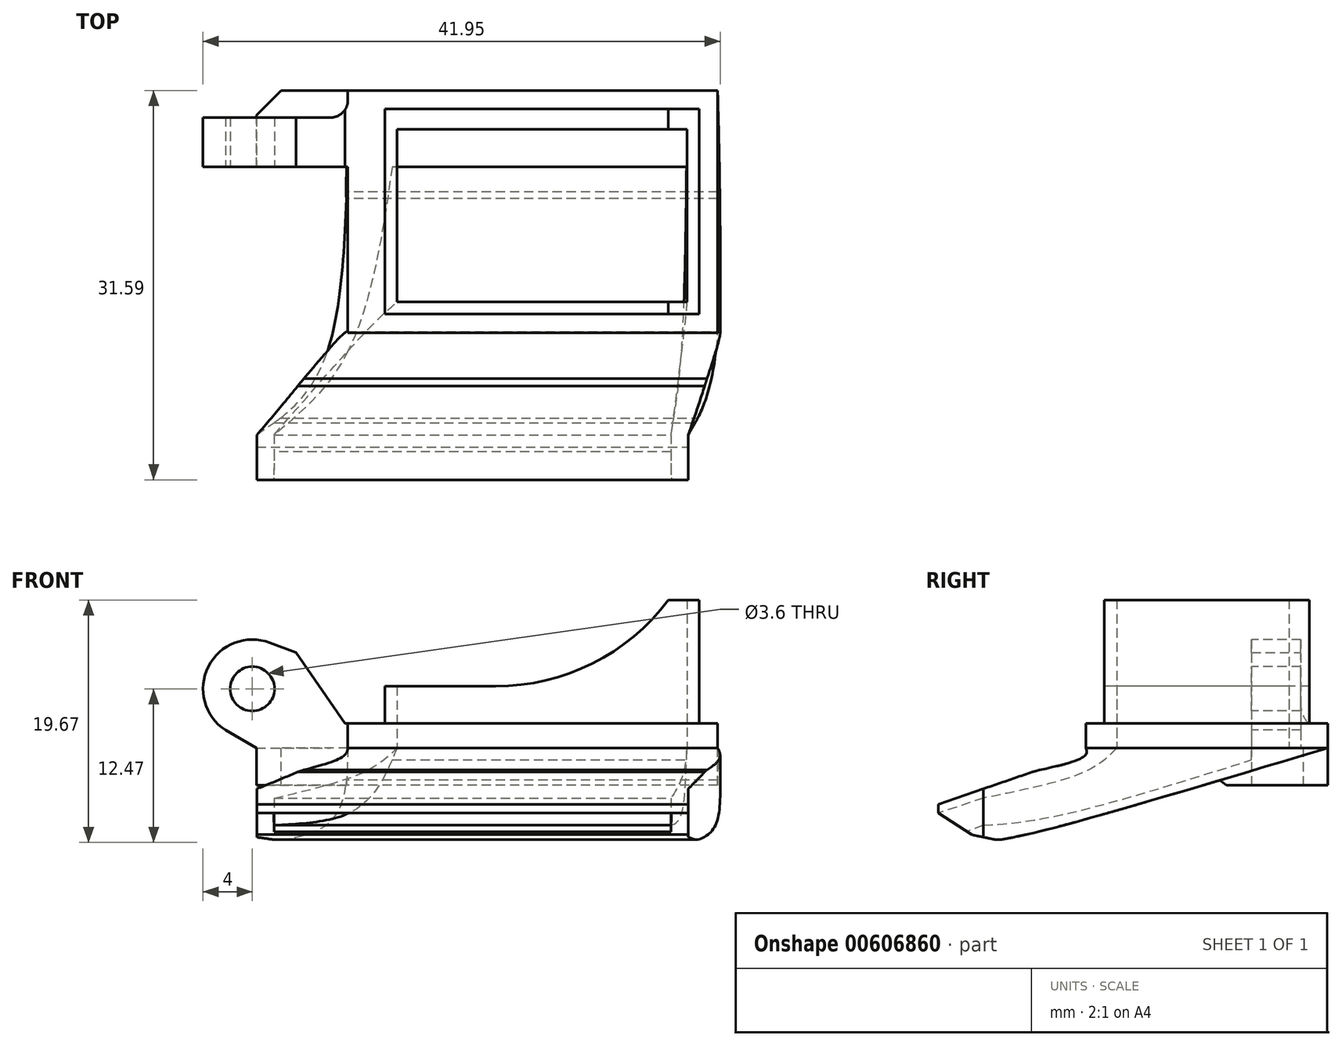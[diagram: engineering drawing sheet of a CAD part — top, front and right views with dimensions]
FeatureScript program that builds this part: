
annotation { "Feature Type Name" : "Feature", "Feature Type Description" : "" }
export const myFeature = defineFeature(function(context is Context, id is Id, definition is map)
    precondition{}
    {
        {
            var Q0;
            Q0=qCreatedBy(makeId("Top.planeOp"),FACE);
            var sketch = newSketch(context, id + "F0", { "sketchPlane" : qUnion([Q0])});
            skLineSegment(sketch, "E0.bottom", {"start": v(-12.75, 8.32) * mm, "end": v(12.75, 8.32) * mm});
            skLineSegment(sketch, "E0.top", {"start": v(-12.75, -8.32) * mm, "end": v(12.75, -8.32) * mm});
            skLineSegment(sketch, "E0.left", {"start": v(-12.75, 8.32) * mm, "end": v(-12.75, -8.32) * mm});
            skLineSegment(sketch, "E0.right", {"start": v(12.75, 8.32) * mm, "end": v(12.75, -8.32) * mm});
            skLineSegment(sketch, "E1.bottom", {"start": v(-11.75, 6.68) * mm, "end": v(11.75, 6.68) * mm});
            skLineSegment(sketch, "E1.top", {"start": v(-11.75, -7.32) * mm, "end": v(11.75, -7.32) * mm});
            skLineSegment(sketch, "E1.left", {"start": v(-11.75, 6.68) * mm, "end": v(-11.75, -7.32) * mm});
            skLineSegment(sketch, "E1.right", {"start": v(11.75, 6.68) * mm, "end": v(11.75, -7.32) * mm});
            skSolve(sketch);
        }
        {
            var Q0;
            Q0=makeQuery(id+"F0.imprint","IMPRINT",FACE,{"disambiguationData":[TD([[makeQuery(id+"F0.imprint","IMPRINT",EDGE,{"derivedFrom":sQuery(id+"F0.wireOp",EDGE,"E0.bottom")}),-1.0]])]});
            extrude(context, id + "F1", {"entities" : qUnion([Q0]), "depth" : 10 * mm, "offsetDistance" : 25 * mm});
        }
        {
            var Q0;
            Q0=makeQuery(id+"F1.opExtrude","SWEPT_FACE",FACE,{"disambiguationData":[OSD([sQuery(id+"F0.wireOp",EDGE,"E0.top")])]});
            var sketch = newSketch(context, id + "F2", { "sketchPlane" : qUnion([Q0])});
            skLineSegment(sketch, "E2", {"start": v(10.25, 10) * mm, "end": v(-3.75, 3) * mm, "construction": true});
            skLineSegment(sketch, "E3", {"start": v(-3.75, 3) * mm, "end": v(-12.75, 3) * mm});
            skArc(sketch, "E4", {"start": v(-3.75, 3) * mm, "mid": v(4.08, 4.85) * mm, "end": v(10.25, 10) * mm});
            skLineSegment(sketch, "E5", {"start": v(-12.75, 3) * mm, "end": v(-12.75, 10) * mm});
            skLineSegment(sketch, "E6", {"start": v(-12.75, 10) * mm, "end": v(10.25, 10) * mm});
            skSolve(sketch);
        }
        {
            var Q0;
            Q0=qSketchRegion(id+"F2",true);
            extrude(context, id + "F3", {"entities" : qUnion([Q0]), "operationType" : NewBodyOperationType.REMOVE, "oppositeDirection" : true, "depth" : 25 * mm, "offsetDistance" : 25 * mm});
        }
        {
            var Q0;
            Q0=makeQuery(id+"F1.opExtrude","CAP_FACE",FACE,{"disambiguationData":[OSD([sQuery(id+"F0.wireOp",EDGE,"E0.bottom"),sQuery(id+"F0.wireOp",EDGE,"E0.top"),sQuery(id+"F0.wireOp",EDGE,"E0.left"),sQuery(id+"F0.wireOp",EDGE,"E0.right"),sQuery(id+"F0.wireOp",EDGE,"E1.bottom"),sQuery(id+"F0.wireOp",EDGE,"E1.top"),sQuery(id+"F0.wireOp",EDGE,"E1.left"),sQuery(id+"F0.wireOp",EDGE,"E1.right")])],"isStart":true});
            var sketch = newSketch(context, id + "F4", { "sketchPlane" : qUnion([Q0])});
            skLineSegment(sketch, "E7.0", {"start": v(-15.75, 9.82) * mm, "end": v(14.25, 9.82) * mm});
            skLineSegment(sketch, "E7.1", {"start": v(-15.75, 9.82) * mm, "end": v(-15.75, -9.82) * mm});
            skLineSegment(sketch, "E7.2", {"start": v(-15.75, -9.82) * mm, "end": v(14.25, -9.82) * mm});
            skLineSegment(sketch, "E7.3", {"start": v(14.25, 9.82) * mm, "end": v(14.25, -9.82) * mm});
            skLineSegment(sketch, "E8.bottom", {"start": v(-11.75, -6.68) * mm, "end": v(11.75, -6.68) * mm});
            skLineSegment(sketch, "E8.top", {"start": v(-11.75, 7.32) * mm, "end": v(11.75, 7.32) * mm});
            skLineSegment(sketch, "E8.left", {"start": v(-11.75, -6.68) * mm, "end": v(-11.75, 7.32) * mm});
            skLineSegment(sketch, "E8.right", {"start": v(11.75, -6.68) * mm, "end": v(11.75, 7.32) * mm});
            skSolve(sketch);
        }
        {
            var Q0;
            Q0=qSketchRegion(id+"F4",true);
            extrude(context, id + "F5", {"entities" : qUnion([Q0]), "operationType" : NewBodyOperationType.ADD, "depth" : 2 * mm, "offsetDistance" : 25 * mm});
        }
        {
            var Q0;
            Q0=makeQuery(id+"F1.opExtrude","SWEPT_FACE",FACE,{"disambiguationData":[OSD([sQuery(id+"F0.wireOp",EDGE,"E0.top")])]});
            cPlane(context, id + "F6", {"entities" : qUnion([Q0]), "cplaneType" : CPlaneType.OFFSET, "offset" : 11.95 * mm, "oppositeDirection" : true, "width" : 150 * mm, "height" : 150 * mm});
        }
        {
            var Q0;
            Q0=qCreatedBy(id+"F6.planeOp",FACE);
            var sketch = newSketch(context, id + "F7", { "sketchPlane" : qUnion([Q0])});
            skCircle(sketch, "E9", {"center": v(-23.5, 2.8) * mm, "radius": 1.8 * mm});
            skArc(sketch, "E10", {"start": v(-22.08, 6.54) * mm, "mid": v(-27.07, 4.6) * mm, "end": v(-25.68, -0.56) * mm});
            skLineSegment(sketch, "E11", {"start": v(-12.75, 3) * mm, "end": v(-22.08, 6.54) * mm});
            skLineSegment(sketch, "E12", {"start": v(-12.75, 3) * mm, "end": v(-12.75, 0) * mm});
            skLineSegment(sketch, "E13", {"start": v(-25.68, -0.56) * mm, "end": v(-23.17, -2) * mm});
            skLineSegment(sketch, "E14", {"start": v(-23.17, -2) * mm, "end": v(-15.75, -2) * mm});
            skLineSegment(sketch, "E15", {"start": v(-12.75, 0) * mm, "end": v(-15.75, 0) * mm});
            skLineSegment(sketch, "E16", {"start": v(-15.75, 0) * mm, "end": v(-15.75, -2) * mm});
            skSolve(sketch);
        }
        {
            var Q0;
            Q0=qSketchRegion(id+"F7",true);
            extrude(context, id + "F8", {"entities" : qUnion([Q0]), "oppositeDirection" : true, "depth" : 4 * mm, "offsetDistance" : 25 * mm});
        }
        {
            var Q0;
            Q0=makeQuery(id+"F1.opExtrude","SWEPT_FACE",FACE,{"disambiguationData":[OSD([sQuery(id+"F0.wireOp",EDGE,"E0.top")])]});
            cPlane(context, id + "F9", {"entities" : qUnion([Q0]), "cplaneType" : CPlaneType.OFFSET, "offset" : 9.8 * mm, "width" : 150 * mm, "height" : 150 * mm});
        }
        {
            var Q0;
            Q0=makeQuery(id+"F21.boolean.opBoolean","MERGE",FACE,{"derivedFrom":[makeQuery(id+"F5.opExtrude","CAP_FACE",FACE,{"disambiguationData":[OSD([sQuery(id+"F4.wireOp",EDGE,"E7.0"),sQuery(id+"F4.wireOp",EDGE,"E7.1"),sQuery(id+"F4.wireOp",EDGE,"E7.2"),sQuery(id+"F4.wireOp",EDGE,"E7.3"),sQuery(id+"F4.wireOp",EDGE,"E8.bottom"),sQuery(id+"F4.wireOp",EDGE,"E8.top"),sQuery(id+"F4.wireOp",EDGE,"E8.left"),sQuery(id+"F4.wireOp",EDGE,"E8.right")])],"isStart":true})],"fromTools":[makeQuery(id+"F21.opExtrude","SWEPT_FACE",FACE,{"disambiguationData":[OSD([sQuery(id+"F20.wireOp",EDGE,"E25.bottom")])]})]});
            cPlane(context, id + "F10", {"entities" : qUnion([Q0]), "cplaneType" : CPlaneType.OFFSET, "offset" : 5 * mm, "oppositeDirection" : true, "width" : 150 * mm, "height" : 150 * mm});
        }
        {
            var Q0;
            Q0=qCreatedBy(id+"F9.planeOp",FACE);
            var sketch = newSketch(context, id + "F11", { "sketchPlane" : qUnion([Q0])});
            skLineSegment(sketch, "E17.bottom", {"start": v(-6.25, -8.67) * mm, "end": v(-21.25, -8.67) * mm});
            skLineSegment(sketch, "E17.top", {"start": v(-6.25, -3.67) * mm, "end": v(-21.25, -3.67) * mm});
            skLineSegment(sketch, "E17.left", {"start": v(-6.25, -8.67) * mm, "end": v(-6.25, -3.67) * mm});
            skLineSegment(sketch, "E17.right", {"start": v(-21.25, -8.67) * mm, "end": v(-21.25, -3.67) * mm});
            skPoint(sketch, "E17.middle", {"position": v(-13.75, -6.17) * mm});
            skLineSegment(sketch, "E18.0", {"start": v(-20.65, -8.07) * mm, "end": v(-20.65, -4.27) * mm});
            skLineSegment(sketch, "E18.1", {"start": v(-6.85, -8.07) * mm, "end": v(-20.65, -8.07) * mm});
            skLineSegment(sketch, "E18.2", {"start": v(-6.85, -8.07) * mm, "end": v(-6.85, -4.27) * mm});
            skLineSegment(sketch, "E18.3", {"start": v(-6.85, -4.27) * mm, "end": v(-20.65, -4.27) * mm});
            skSolve(sketch);
        }
        {
            var Q0;
            Q0=makeQuery(id+"F5.opExtrude","CAP_FACE",FACE,{"disambiguationData":[OSD([sQuery(id+"F4.wireOp",EDGE,"E7.0"),sQuery(id+"F4.wireOp",EDGE,"E7.1"),sQuery(id+"F4.wireOp",EDGE,"E7.2"),sQuery(id+"F4.wireOp",EDGE,"E7.3"),sQuery(id+"F4.wireOp",EDGE,"E8.bottom"),sQuery(id+"F4.wireOp",EDGE,"E8.top"),sQuery(id+"F4.wireOp",EDGE,"E8.left"),sQuery(id+"F4.wireOp",EDGE,"E8.right")])],"isStart":false});
            var sketch = newSketch(context, id + "F12", { "sketchPlane" : qUnion([Q0])});
            skLineSegment(sketch, "E19.0", {"start": v(-15.75, 9.82) * mm, "end": v(-15.75, -9.82) * mm});
            skLineSegment(sketch, "E19.3", {"start": v(-15.75, 9.82) * mm, "end": v(14.25, 9.82) * mm});
            skLineSegment(sketch, "E19.4", {"start": v(-15.75, -9.82) * mm, "end": v(14.25, -9.82) * mm});
            skLineSegment(sketch, "E19.7", {"start": v(14.25, 9.82) * mm, "end": v(14.25, -9.82) * mm});
            skSolve(sketch);
        }
        {
            var Q0;
            Q0=qCreatedBy(makeId("Front.planeOp"),FACE);
            cPlane(context, id + "F13", {"entities" : qUnion([Q0]), "cplaneType" : CPlaneType.OFFSET, "offset" : 11.3 * mm, "width" : 150 * mm, "height" : 150 * mm});
        }
        {
            var Q0;
            Q0=qCreatedBy(id+"F13.planeOp",FACE);
            var sketch = newSketch(context, id + "F14", { "sketchPlane" : qUnion([Q0])});
            skLineSegment(sketch, "E20.bottom", {"start": v(14.1, -3.25) * mm, "end": v(-17.4, -3.25) * mm});
            skLineSegment(sketch, "E20.top", {"start": v(14.1, -8.18) * mm, "end": v(-17.4, -8.18) * mm});
            skLineSegment(sketch, "E20.left", {"start": v(14.1, -3.25) * mm, "end": v(14.1, -8.18) * mm});
            skLineSegment(sketch, "E20.right", {"start": v(-17.4, -3.25) * mm, "end": v(-17.4, -8.18) * mm});
            skSolve(sketch);
        }
        {
            var Q0;
            Q0=qCreatedBy(id+"F9.planeOp",FACE);
            var sketch = newSketch(context, id + "F15", { "sketchPlane" : qUnion([Q0])});
            skLineSegment(sketch, "E21.bottom", {"start": v(-23.14, -4.67) * mm, "end": v(11.86, -4.67) * mm});
            skLineSegment(sketch, "E21.top", {"start": v(-23.14, -9.67) * mm, "end": v(11.86, -9.67) * mm});
            skLineSegment(sketch, "E21.left", {"start": v(-23.14, -4.67) * mm, "end": v(-23.14, -9.67) * mm});
            skLineSegment(sketch, "E21.right", {"start": v(11.86, -4.67) * mm, "end": v(11.86, -9.67) * mm});
            skLineSegment(sketch, "E22.0", {"start": v(-21.74, -6.07) * mm, "end": v(-21.74, -8.27) * mm, "construction": true});
            skLineSegment(sketch, "E22.1", {"start": v(-21.74, -6.07) * mm, "end": v(10.46, -6.07) * mm, "construction": true});
            skLineSegment(sketch, "E22.2", {"start": v(10.46, -6.07) * mm, "end": v(10.46, -8.27) * mm, "construction": true});
            skLineSegment(sketch, "E22.3", {"start": v(-21.74, -8.27) * mm, "end": v(10.46, -8.27) * mm, "construction": true});
            skSolve(sketch);
        }
        {
            var Q1;
            Q1=qSketchRegion(id+"F15",true);
            var Q2;
            Q2=qSketchRegion(id+"F14",true);
            var Q3;
            Q3=qSketchRegion(id+"F12",true);
            var Q4;
            Q4=sQuery(id+"F15.wireOp",VERTEX,"E21.right.start");
            var Q5;
            Q5=sQuery(id+"F14.wireOp",VERTEX,"E20.left.start");
            var Q6;
            Q6=sQuery(id+"F12.wireOp",VERTEX,"E19.7.start");
            loft(context, id + "F16", {"operationType" : NewBodyOperationType.ADD, "sheetProfilesArray" : [{ "sheetProfileEntities" : qUnion([Q1]) }, { "sheetProfileEntities" : qUnion([Q2]) }, { "sheetProfileEntities" : qUnion([Q3]) }], "matchConnections" : true, "connections" : [{ "connectionEntities" : qUnion([Q4, Q5, Q6]), "connectionEdgeQueries" : qUnion([]), "connectionEdgeParameters" : [] }]});
        }
        {
            var Q0;
            Q0=qCreatedBy(id+"F13.planeOp",FACE);
            var sketch = newSketch(context, id + "F17", { "sketchPlane" : qUnion([Q0])});
            skLineSegment(sketch, "E23.bottom", {"start": v(-15.73, -4.47) * mm, "end": v(11.32, -4.47) * mm});
            skLineSegment(sketch, "E23.top", {"start": v(-15.73, -7.32) * mm, "end": v(11.32, -7.32) * mm});
            skLineSegment(sketch, "E23.left", {"start": v(-15.73, -4.47) * mm, "end": v(-15.73, -7.32) * mm});
            skLineSegment(sketch, "E23.right", {"start": v(11.32, -4.47) * mm, "end": v(11.32, -7.32) * mm});
            skSolve(sketch);
        }
        {
            var Q0;
            Q0=makeQuery(id+"F16.opLoft","CAP_FACE",FACE,{"disambiguationData":[OSD([makeQuery(id+"F12.imprint","IMPRINT",FACE,{"disambiguationData":[TD([[makeQuery(id+"F12.imprint","IMPRINT",EDGE,{"derivedFrom":makeQuery(id+"F5.opExtrude","CAP_EDGE",EDGE,{"disambiguationData":[OSD([sQuery(id+"F4.wireOp",EDGE,"E8.bottom")])],"isStart":false})}),1.0]])]})])],"isStart":true});
            var sketch = newSketch(context, id + "F18", { "sketchPlane" : qUnion([Q0])});
            skLineSegment(sketch, "E24.bottom", {"start": v(-11.75, 6.68) * mm, "end": v(11.75, 6.68) * mm});
            skLineSegment(sketch, "E24.top", {"start": v(-11.75, -7.32) * mm, "end": v(11.75, -7.32) * mm});
            skLineSegment(sketch, "E24.left", {"start": v(-11.75, 6.68) * mm, "end": v(-11.75, -7.32) * mm});
            skLineSegment(sketch, "E24.right", {"start": v(11.75, 6.68) * mm, "end": v(11.75, -7.32) * mm});
            skSolve(sketch);
        }
        {
            var Q0;
            Q0=makeQuery(id+"F11.imprint","IMPRINT",FACE,{"disambiguationData":[TD([[makeQuery(id+"F11.imprint","IMPRINT",EDGE,{"derivedFrom":sQuery(id+"F11.wireOp",EDGE,"E17.bottom")}),-1.0]])]});
            cPlane(context, id + "F19", {"entities" : qUnion([Q0]), "cplaneType" : CPlaneType.OFFSET, "offset" : 3.65 * mm, "width" : 150 * mm, "height" : 150 * mm});
        }
        {
            var Q0;
            Q0=makeQuery(id+"F8.opExtrude","CAP_FACE",FACE,{"disambiguationData":[OSD([sQuery(id+"F7.wireOp",EDGE,"E9"),sQuery(id+"F7.wireOp",EDGE,"E10"),sQuery(id+"F7.wireOp",EDGE,"E11"),sQuery(id+"F7.wireOp",EDGE,"E12"),sQuery(id+"F7.wireOp",EDGE,"E13"),sQuery(id+"F7.wireOp",EDGE,"E14"),sQuery(id+"F7.wireOp",EDGE,"E15"),sQuery(id+"F7.wireOp",EDGE,"E16")])],"isStart":true});
            var sketch = newSketch(context, id + "F20", { "sketchPlane" : qUnion([Q0])});
            skLineSegment(sketch, "E25.bottom", {"start": v(-15.75, 0) * mm, "end": v(-12.75, 0) * mm});
            skLineSegment(sketch, "E25.top", {"start": v(-15.75, 4.97) * mm, "end": v(-12.75, 4.97) * mm});
            skLineSegment(sketch, "E25.left", {"start": v(-15.75, 0) * mm, "end": v(-15.75, 4.97) * mm});
            skLineSegment(sketch, "E25.right", {"start": v(-12.75, 0) * mm, "end": v(-12.75, 4.97) * mm});
            skSolve(sketch);
        }
        {
            var Q0;
            Q0 = qSketchRegion(id + "F20", true);
            extrude(context, id + "F21", {"entities" : qUnion([Q0]), "operationType" : NewBodyOperationType.REMOVE, "oppositeDirection" : true, "depth" : 25 * mm, "offsetDistance" : 25 * mm});
        }
        {
            var Q0;
            Q0=makeQuery(id+"F21.boolean.opBoolean","INTERSECT",EDGE,{"derivedFrom":[makeQuery(id+"F8.opExtrude","SWEPT_FACE",FACE,{"disambiguationData":[OSD([sQuery(id+"F7.wireOp",EDGE,"E11")])]}),makeQuery(id+"F21.opExtrude","SWEPT_FACE",FACE,{"disambiguationData":[OSD([sQuery(id+"F20.wireOp",EDGE,"E25.left")])]})]});
            chamfer(context, id + "F22", {"entities" : qUnion([Q0]), "width" : 6.5 * mm, "tangentPropagation" : true});
        }
        {
            var Q0;
            Q0=makeQuery(id+"F8.opExtrude","CAP_EDGE",EDGE,{"disambiguationData":[OSD([sQuery(id+"F7.wireOp",EDGE,"E16")])],"isStart":false});
            fillet(context, id + "F23", {"entities" : qUnion([Q0]), "radius" : 1.4 * mm, "tangentPropagation" : true, "allowEdgeOverflow" : false});
        }
        {
            var Q0;
            Q0=makeQuery(id+"F8.opExtrude","CAP_FACE",FACE,{"disambiguationData":[OSD([sQuery(id+"F7.wireOp",EDGE,"E9"),sQuery(id+"F7.wireOp",EDGE,"E10"),sQuery(id+"F7.wireOp",EDGE,"E11"),sQuery(id+"F7.wireOp",EDGE,"E12"),sQuery(id+"F7.wireOp",EDGE,"E13"),sQuery(id+"F7.wireOp",EDGE,"E14"),sQuery(id+"F7.wireOp",EDGE,"E15"),sQuery(id+"F7.wireOp",EDGE,"E16")])],"isStart":false});
            var sketch = newSketch(context, id + "F24", { "sketchPlane" : qUnion([Q0])});
            skLineSegment(sketch, "E26.0", {"start": v(15.75, -2) * mm, "end": v(15.75, 0) * mm, "construction": true});
            skLineSegment(sketch, "E27.0", {"start": v(23.17, -2) * mm, "end": v(19.3, -2) * mm, "construction": true});
            skLineSegment(sketch, "E28", {"start": v(15.75, -2) * mm, "end": v(23.17, -2) * mm});
            skLineSegment(sketch, "E29", {"start": v(23.17, -5.03) * mm, "end": v(15.75, -5.03) * mm});
            skLineSegment(sketch, "E30", {"start": v(15.75, -5.03) * mm, "end": v(15.75, -2) * mm});
            skLineSegment(sketch, "E31", {"start": v(23.17, -2) * mm, "end": v(23.17, -5.03) * mm});
            skSolve(sketch);
        }
        {
            var Q0;
            Q0 = qSketchRegion(id + "F24", true);
            extrude(context, id + "F25", {"entities" : qUnion([Q0]), "operationType" : NewBodyOperationType.ADD, "oppositeDirection" : true, "depth" : 4 * mm, "offsetDistance" : 25 * mm});
        }
        {
            var Q0;
            Q0=makeQuery(id+"F15.imprint","IMPRINT",FACE,{"disambiguationData":[TD([[makeQuery(id+"F15.imprint","IMPRINT",EDGE,{"derivedFrom":sQuery(id+"F15.wireOp",EDGE,"E21.bottom")}),-1.0]])]});
            var sketch = newSketch(context, id + "F26", { "sketchPlane" : qUnion([Q0])});
            skLineSegment(sketch, "E32.0", {"start": v(-21.74, -6.07) * mm, "end": v(10.46, -6.07) * mm});
            skLineSegment(sketch, "E33.0", {"start": v(-21.74, -6.07) * mm, "end": v(-21.74, -8.27) * mm});
            skLineSegment(sketch, "E34.0", {"start": v(-21.74, -8.27) * mm, "end": v(10.46, -8.27) * mm});
            skLineSegment(sketch, "E35.0", {"start": v(10.46, -6.07) * mm, "end": v(10.46, -8.27) * mm});
            skSolve(sketch);
        }
        {
            var Q1;
            Q1=makeQuery(id+"F18.imprint","IMPRINT",FACE,{"disambiguationData":[TD([[makeQuery(id+"F18.imprint","IMPRINT",EDGE,{"derivedFrom":sQuery(id+"F18.wireOp",EDGE,"E24.bottom")}),-1.0]])]});
            var Q2;
            Q2 = qSketchRegion(id + "F17", true);
            var Q3;
            Q3 = qSketchRegion(id + "F26", true);
            loft(context, id + "F27", {"operationType" : NewBodyOperationType.REMOVE, "sheetProfilesArray" : [{ "sheetProfileEntities" : qUnion([Q1]) }, { "sheetProfileEntities" : qUnion([Q2]) }, { "sheetProfileEntities" : qUnion([Q3]) }]});
        }
        {
            var Q0;
            Q0=qCreatedBy(id+"F19.planeOp",FACE);
            var sketch = newSketch(context, id + "F28", { "sketchPlane" : qUnion([Q0])});
            skLineSegment(sketch, "E36.0.0", {"start": v(-23.14, -4.67) * mm, "end": v(-23.14, -9.67) * mm});
            skLineSegment(sketch, "E36.0.1", {"start": v(-23.14, -9.67) * mm, "end": v(11.86, -9.67) * mm});
            skLineSegment(sketch, "E36.0.2", {"start": v(11.86, -9.67) * mm, "end": v(11.86, -4.67) * mm});
            skLineSegment(sketch, "E36.0.3", {"start": v(11.86, -4.67) * mm, "end": v(-23.14, -4.67) * mm});
            skSolve(sketch);
        }
        {
            var Q1;
            Q1=makeQuery(id+"F15.imprint","IMPRINT",FACE,{"disambiguationData":[TD([[makeQuery(id+"F15.imprint","IMPRINT",EDGE,{"derivedFrom":sQuery(id+"F15.wireOp",EDGE,"E21.bottom")}),-1.0]])]});
            var Q2;
            Q2=makeQuery(id+"F28.imprint","IMPRINT",FACE,{"disambiguationData":[TD([[makeQuery(id+"F28.imprint","IMPRINT",EDGE,{"derivedFrom":sQuery(id+"F28.wireOp",EDGE,"E36.0.0")}),1.0]])]});
            loft(context, id + "F29", {"operationType" : NewBodyOperationType.ADD, "sheetProfilesArray" : [{ "sheetProfileEntities" : qUnion([Q1]) }, { "sheetProfileEntities" : qUnion([Q2]) }]});
        }
        {
            var Q0;
            Q0=makeQuery(id+"F28.imprint","IMPRINT",FACE,{"disambiguationData":[TD([[makeQuery(id+"F28.imprint","IMPRINT",EDGE,{"derivedFrom":sQuery(id+"F28.wireOp",EDGE,"E36.0.0")}),1.0]])]});
            var sketch = newSketch(context, id + "F30", { "sketchPlane" : qUnion([Q0])});
            skLineSegment(sketch, "E37.bottom", {"start": v(-21.75, -7.3) * mm, "end": v(10.48, -7.3) * mm});
            skLineSegment(sketch, "E37.top", {"start": v(-21.75, -9.67) * mm, "end": v(10.48, -9.67) * mm});
            skLineSegment(sketch, "E37.left", {"start": v(-21.75, -7.3) * mm, "end": v(-21.75, -9.67) * mm});
            skLineSegment(sketch, "E37.right", {"start": v(10.48, -7.3) * mm, "end": v(10.48, -9.67) * mm});
            skSolve(sketch);
        }
        {
            var Q0;
            Q0=qCreatedBy(id+"F9.planeOp",FACE);
            var sketch = newSketch(context, id + "F31", { "sketchPlane" : qUnion([Q0])});
            skLineSegment(sketch, "E38.0", {"start": v(-21.74, -6.07) * mm, "end": v(-21.74, -8.27) * mm});
            skLineSegment(sketch, "E39.0", {"start": v(-21.74, -6.07) * mm, "end": v(10.46, -6.07) * mm});
            skLineSegment(sketch, "E40.0", {"start": v(-21.74, -8.27) * mm, "end": v(10.46, -8.27) * mm});
            skLineSegment(sketch, "E41.0", {"start": v(10.46, -6.07) * mm, "end": v(10.46, -8.27) * mm});
            skSolve(sketch);
        }
        {
            var Q1;
            Q1 = qSketchRegion(id + "F31", true);
            var Q2;
            Q2 = qSketchRegion(id + "F30", true);
            loft(context, id + "F32", {"operationType" : NewBodyOperationType.REMOVE, "sheetProfilesArray" : [{ "sheetProfileEntities" : qUnion([Q1]) }, { "sheetProfileEntities" : qUnion([Q2]) }]});
        }
        {
            var Q0;
            Q0=makeQuery(id+"F29.opLoft","SWEPT_FACE",FACE,{"disambiguationData":[OSD([sQuery(id+"F15.wireOp",EDGE,"E21.bottom"),sQuery(id+"F15.wireOp",EDGE,"E21.top"),sQuery(id+"F15.wireOp",EDGE,"E21.right"),sQuery(id+"F28.wireOp",EDGE,"E36.0.1"),sQuery(id+"F28.wireOp",EDGE,"E36.0.2"),sQuery(id+"F28.wireOp",EDGE,"E36.0.3")])]});
            var sketch = newSketch(context, id + "F33", { "sketchPlane" : qUnion([Q0])});
            skLineSegment(sketch, "E42.0", {"start": v(-21.77, -9.67) * mm, "end": v(-21.77, -7.3) * mm});
            skLineSegment(sketch, "E43.0", {"start": v(-18.12, -9.67) * mm, "end": v(-21.77, -9.67) * mm});
            skLineSegment(sketch, "E44", {"start": v(-21.77, -7.3) * mm, "end": v(-18.12, -9.67) * mm});
            skSolve(sketch);
        }
        {
            var Q0;
            Q0 = qSketchRegion(id + "F33", true);
            extrude(context, id + "F34", {"entities" : qUnion([Q0]), "operationType" : NewBodyOperationType.REMOVE, "endBound" : BoundingType.UP_TO_NEXT, "oppositeDirection" : true, "depth" : 25 * mm, "offsetDistance" : 25 * mm});
        }
        {
            var Q0;
            {var subQ0=sQuery(id+"F15.wireOp",EDGE,"E21.right");var subQ1=sQuery(id+"F15.wireOp",EDGE,"E21.top");var subQ2=sQuery(id+"F15.wireOp",EDGE,"E21.left");Q0=makeQuery(id+"F34.boolean.opBoolean","MERGE",EDGE,{"derivedFrom":[makeQuery(id+"F29.boolean.opBoolean","MERGE",EDGE,{"derivedFrom":[makeQuery(id+"F16.opLoft","MID_CAP_EDGE",EDGE,{"disambiguationData":[OSD([subQ1,subQ2,subQ0])],"capPos":0.0}),makeQuery(id+"F29.opLoft","MID_CAP_EDGE",EDGE,{"disambiguationData":[OSD([subQ1,subQ2,subQ0])],"capPos":0.0})]})],"fromTools":[makeQuery(id+"F34.opExtrude","SWEPT_EDGE",EDGE,{"disambiguationData":[OSD([sQuery(id+"F15.wireOp",EDGE,"E21.bottom"),subQ1,subQ0,sQuery(id+"F33.wireOp",EDGE,"E43.0"),sQuery(id+"F33.wireOp",EDGE,"E44")])]})]});}
            chamfer(context, id + "F35", {"entities" : qUnion([Q0]), "width" : 3 * mm, "tangentPropagation" : true});
        }
        {
            var Q0;
            Q0=makeQuery(id+"F29.opLoft","MID_CAP_EDGE",EDGE,{"disambiguationData":[OSD([sQuery(id+"F28.wireOp",EDGE,"E36.0.0"),sQuery(id+"F28.wireOp",EDGE,"E36.0.2"),sQuery(id+"F28.wireOp",EDGE,"E36.0.3")])],"capPos":1.0});
            chamfer(context, id + "F36", {"entities" : qUnion([Q0]), "chamferType" : ChamferType.OFFSET_ANGLE, "width" : 1.9 * mm, "oppositeDirection" : false, "angle" : 71 * degree, "tangentPropagation" : true});
        }
        {
            var Q0;
            {var subQ0=sQuery(id+"F15.wireOp",EDGE,"E21.right");var subQ1=sQuery(id+"F15.wireOp",EDGE,"E21.left");var subQ2=sQuery(id+"F15.wireOp",EDGE,"E21.top");Q0=makeQuery(id+"F35.opChamfer","BLEND_EDGE",EDGE,{"blendedFrom":[makeQuery(id+"F34.boolean.opBoolean","MERGE",EDGE,{"derivedFrom":[makeQuery(id+"F29.boolean.opBoolean","MERGE",EDGE,{"derivedFrom":[makeQuery(id+"F16.opLoft","MID_CAP_EDGE",EDGE,{"disambiguationData":[OSD([subQ2,subQ1,subQ0])],"capPos":0.0}),makeQuery(id+"F29.opLoft","MID_CAP_EDGE",EDGE,{"disambiguationData":[OSD([subQ2,subQ1,subQ0])],"capPos":0.0})]})],"fromTools":[makeQuery(id+"F34.opExtrude","SWEPT_EDGE",EDGE,{"disambiguationData":[OSD([sQuery(id+"F15.wireOp",EDGE,"E21.bottom"),subQ2,subQ0,sQuery(id+"F33.wireOp",EDGE,"E43.0"),sQuery(id+"F33.wireOp",EDGE,"E44")])]})]}),makeQuery(id+"F16.opLoft","SWEPT_FACE",FACE,{"disambiguationData":[OSD([sQuery(id+"F12.wireOp",EDGE,"E19.0"),sQuery(id+"F12.wireOp",EDGE,"E19.4"),sQuery(id+"F12.wireOp",EDGE,"E19.7"),sQuery(id+"F14.wireOp",EDGE,"E20.top"),sQuery(id+"F14.wireOp",EDGE,"E20.left"),sQuery(id+"F14.wireOp",EDGE,"E20.right"),subQ2,subQ1,subQ0])]})],"blendedInto":[makeQuery(id+"F16.opLoft","SWEPT_FACE",FACE,{"disambiguationData":[OSD([sQuery(id+"F12.wireOp",EDGE,"E19.0"),sQuery(id+"F12.wireOp",EDGE,"E19.4"),sQuery(id+"F12.wireOp",EDGE,"E19.7"),sQuery(id+"F14.wireOp",EDGE,"E20.top"),sQuery(id+"F14.wireOp",EDGE,"E20.left"),sQuery(id+"F14.wireOp",EDGE,"E20.right"),subQ2,subQ1,subQ0])]})]});}
            chamfer(context, id + "F37", {"entities" : qUnion([Q0]), "width" : 1 * mm, "tangentPropagation" : true});
        }
        {
            var Q0;
            Q0=makeQuery(id+"F36.opChamfer","BLEND_EDGE",EDGE,{"blendedFrom":[makeQuery(id+"F29.opLoft","MID_CAP_EDGE",EDGE,{"disambiguationData":[OSD([sQuery(id+"F28.wireOp",EDGE,"E36.0.0"),sQuery(id+"F28.wireOp",EDGE,"E36.0.2"),sQuery(id+"F28.wireOp",EDGE,"E36.0.3")])],"capPos":1.0}),makeQuery(id+"F16.opLoft","SWEPT_FACE",FACE,{"disambiguationData":[OSD([sQuery(id+"F12.wireOp",EDGE,"E19.0"),sQuery(id+"F12.wireOp",EDGE,"E19.3"),sQuery(id+"F12.wireOp",EDGE,"E19.7"),sQuery(id+"F14.wireOp",EDGE,"E20.bottom"),sQuery(id+"F14.wireOp",EDGE,"E20.left"),sQuery(id+"F14.wireOp",EDGE,"E20.right"),sQuery(id+"F15.wireOp",EDGE,"E21.bottom"),sQuery(id+"F15.wireOp",EDGE,"E21.left"),sQuery(id+"F15.wireOp",EDGE,"E21.right")])]})],"blendedInto":[makeQuery(id+"F16.opLoft","SWEPT_FACE",FACE,{"disambiguationData":[OSD([sQuery(id+"F12.wireOp",EDGE,"E19.0"),sQuery(id+"F12.wireOp",EDGE,"E19.3"),sQuery(id+"F12.wireOp",EDGE,"E19.7"),sQuery(id+"F14.wireOp",EDGE,"E20.bottom"),sQuery(id+"F14.wireOp",EDGE,"E20.left"),sQuery(id+"F14.wireOp",EDGE,"E20.right"),sQuery(id+"F15.wireOp",EDGE,"E21.bottom"),sQuery(id+"F15.wireOp",EDGE,"E21.left"),sQuery(id+"F15.wireOp",EDGE,"E21.right")])]})]});
            chamfer(context, id + "F38", {"entities" : qUnion([Q0]), "width" : 5 * mm, "tangentPropagation" : true});
        }
        {
            var Q0;
            Q0=makeQuery(id+"F25.opExtrude","SWEPT_FACE",FACE,{"disambiguationData":[OSD([sQuery(id+"F24.wireOp",EDGE,"E31")])]});
            var sketch = newSketch(context, id + "F39", { "sketchPlane" : qUnion([Q0])});
            skPoint(sketch, "E45.0", {"position": v(-9.82, -2) * mm});
            skPoint(sketch, "E46.0", {"position": v(-3.63, -5.03) * mm});
            skLineSegment(sketch, "E47.bottom", {"start": v(-3.63, -5.03) * mm, "end": v(-9.82, -5.03) * mm});
            skLineSegment(sketch, "E47.top", {"start": v(-3.63, -2) * mm, "end": v(-9.82, -2) * mm});
            skLineSegment(sketch, "E47.left", {"start": v(-3.63, -5.03) * mm, "end": v(-3.63, -2) * mm});
            skLineSegment(sketch, "E47.right", {"start": v(-9.82, -5.03) * mm, "end": v(-9.82, -2) * mm});
            skSolve(sketch);
        }
        {
            var Q0;
            Q0 = qSketchRegion(id + "F39", true);
            var Q1;
            Q1=makeQuery(id+"F16.boolean.opBoolean","MERGE",VERTEX,{"derivedFrom":[makeQuery(id+"F5.opExtrude","CAP_VERTEX",VERTEX,{"disambiguationData":[OSD([sQuery(id+"F4.wireOp",EDGE,"E7.2"),sQuery(id+"F4.wireOp",EDGE,"E7.3")])],"isStart":false}),makeQuery(id+"F16.opLoft","MID_CAP_VERTEX",VERTEX,{"disambiguationData":[OSD([sQuery(id+"F12.wireOp",EDGE,"E19.4"),sQuery(id+"F12.wireOp",EDGE,"E19.7")])],"capPos":2.0})]});
            extrude(context, id + "F40", {"entities" : qUnion([Q0]), "operationType" : NewBodyOperationType.ADD, "endBound" : BoundingType.UP_TO_VERTEX, "oppositeDirection" : true, "depth" : 25 * mm, "endBoundEntityVertex" : qUnion([Q1]), "offsetDistance" : 25 * mm});
        }
        {
            var Q0;
            Q0=makeQuery(id+"F40.opExtrude","CAP_EDGE",EDGE,{"disambiguationData":[OSD([sQuery(id+"F39.wireOp",EDGE,"E47.right")])],"isStart":true});
            var Q1;
            Q1=makeQuery(id+"F40.boolean.opBoolean","INTERSECT",EDGE,{"derivedFrom":[makeQuery(id+"F16.opLoft","SWEPT_FACE",FACE,{"disambiguationData":[OSD([sQuery(id+"F12.wireOp",EDGE,"E19.0"),sQuery(id+"F12.wireOp",EDGE,"E19.4"),sQuery(id+"F12.wireOp",EDGE,"E19.7"),sQuery(id+"F14.wireOp",EDGE,"E20.top"),sQuery(id+"F14.wireOp",EDGE,"E20.left"),sQuery(id+"F14.wireOp",EDGE,"E20.right"),sQuery(id+"F15.wireOp",EDGE,"E21.top"),sQuery(id+"F15.wireOp",EDGE,"E21.left"),sQuery(id+"F15.wireOp",EDGE,"E21.right")])]}),makeQuery(id+"F40.opExtrude","SWEPT_FACE",FACE,{"disambiguationData":[OSD([sQuery(id+"F39.wireOp",EDGE,"E47.left")])]})]});
            chamfer(context, id + "F41", {"entities" : qUnion([Q0, Q1]), "width" : 2 * mm, "tangentPropagation" : true});
        }
    });
